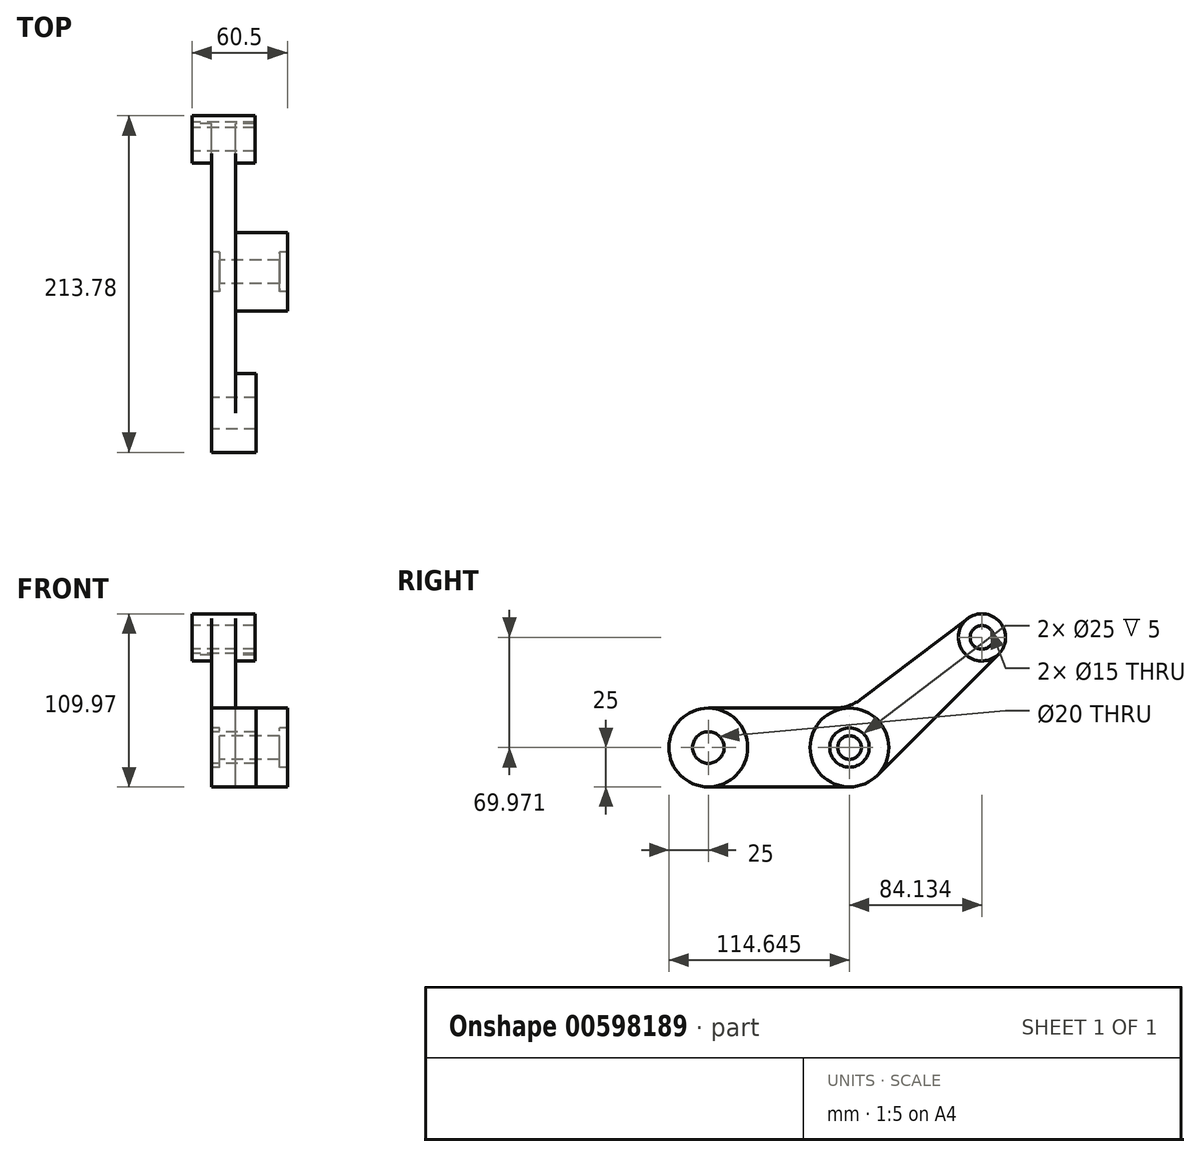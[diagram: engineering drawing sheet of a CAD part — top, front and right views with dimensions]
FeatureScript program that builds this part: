
annotation { "Feature Type Name" : "Feature", "Feature Type Description" : "" }
export const myFeature = defineFeature(function(context is Context, id is Id, definition is map)
    precondition{}
    {
        {
            var Q0;
            Q0=qCreatedBy(makeId("Right.planeOp"),FACE);
            var sketch = newSketch(context, id + "F0", { "sketchPlane" : qUnion([Q0])});
            skLineSegment(sketch, "E0", {"start": v(-100, 0) * mm, "end": v(0, 0) * mm});
            skLineSegment(sketch, "E1", {"start": v(0, 0) * mm, "end": v(84.85, 84.85) * mm});
            skCircle(sketch, "E2", {"center": v(-100, 25) * mm, "radius": 25 * mm});
            skCircle(sketch, "E3", {"center": v(-100, 25) * mm, "radius": 10 * mm});
            skCircle(sketch, "E4", {"center": v(73.78, 94.97) * mm, "radius": 15 * mm});
            skCircle(sketch, "E5", {"center": v(73.78, 94.97) * mm, "radius": 7.5 * mm});
            skCircle(sketch, "E6", {"center": v(-10.36, 25) * mm, "radius": 25 * mm});
            skCircle(sketch, "E7", {"center": v(-10.36, 25) * mm, "radius": 12.5 * mm});
            skCircle(sketch, "E8", {"center": v(-10.36, 25) * mm, "radius": 7.5 * mm});
            skLineSegment(sketch, "E9", {"start": v(-100, 50) * mm, "end": v(-20.44, 50) * mm});
            skLineSegment(sketch, "E10", {"start": v(-2.32, 56.1) * mm, "end": v(64.72, 106.92) * mm});
            skPoint(sketch, "E11.visualSharp", {"position": v(-10.36, 50) * mm});
            skArc(sketch, "E11.filletArc", {"start": v(-20.44, 50) * mm, "mid": v(-10.88, 51.56) * mm, "end": v(-2.32, 56.1) * mm});
            skSolve(sketch);
        }
        {
            var Q0;
            {var subQ3=sQuery(id+"F0.wireOp",EDGE,"E9");Q0=makeQuery(id+"F0.imprint","IMPRINT",FACE,{"disambiguationData":[TD([[makeQuery(id+"F0.imprint","IMPRINT",EDGE,{"derivedFrom":subQ3}),-1.0]])]});}
            extrude(context, id + "F1", {"entities" : qUnion([Q0]), "oppositeDirection" : true, "depth" : 15 * mm, "offsetDistance" : 25 * mm});
        }
        {
            var Q0;
            Q0=makeQuery(id+"F0.imprint","IMPRINT",FACE,{"disambiguationData":[TD([[makeQuery(id+"F0.imprint","IMPRINT",EDGE,{"derivedFrom":sQuery(id+"F0.wireOp",EDGE,"E3")}),-1.0]])]});
            extrude(context, id + "F2", {"entities" : qUnion([Q0]), "operationType" : NewBodyOperationType.ADD, "depth" : 13 * mm, "offsetDistance" : 25 * mm, "hasSecondDirection" : true, "secondDirectionOppositeDirection" : true, "secondDirectionDepth" : 15 * mm});
        }
        {
            var Q0;
            Q0=makeQuery(id+"F0.imprint","IMPRINT",FACE,{"disambiguationData":[TD([[makeQuery(id+"F0.imprint","IMPRINT",EDGE,{"derivedFrom":sQuery(id+"F0.wireOp",EDGE,"E7")}),-1.0]])]});
            extrude(context, id + "F3", {"entities" : qUnion([Q0]), "operationType" : NewBodyOperationType.ADD, "depth" : 33 * mm, "offsetDistance" : 25 * mm, "hasSecondDirection" : true, "secondDirectionOppositeDirection" : true, "secondDirectionDepth" : 15 * mm});
        }
        {
            var Q0;
            Q0=makeQuery(id+"F0.imprint","IMPRINT",FACE,{"disambiguationData":[TD([[makeQuery(id+"F0.imprint","IMPRINT",EDGE,{"derivedFrom":sQuery(id+"F0.wireOp",EDGE,"E7")}),1.0]])]});
            extrude(context, id + "F4", {"entities" : qUnion([Q0]), "operationType" : NewBodyOperationType.ADD, "depth" : 28 * mm, "offsetDistance" : 25 * mm, "hasSecondDirection" : true, "secondDirectionOppositeDirection" : true, "secondDirectionDepth" : 10 * mm});
        }
        {
            var Q0;
            Q0=makeQuery(id+"F0.imprint","IMPRINT",FACE,{"disambiguationData":[TD([[makeQuery(id+"F0.imprint","IMPRINT",EDGE,{"derivedFrom":sQuery(id+"F0.wireOp",EDGE,"E5")}),-1.0]])]});
            extrude(context, id + "F5", {"entities" : qUnion([Q0]), "operationType" : NewBodyOperationType.ADD, "depth" : 12.5 * mm, "offsetDistance" : 25 * mm, "hasSecondDirection" : true, "secondDirectionOppositeDirection" : true, "secondDirectionDepth" : 27.5 * mm});
        }
    });
